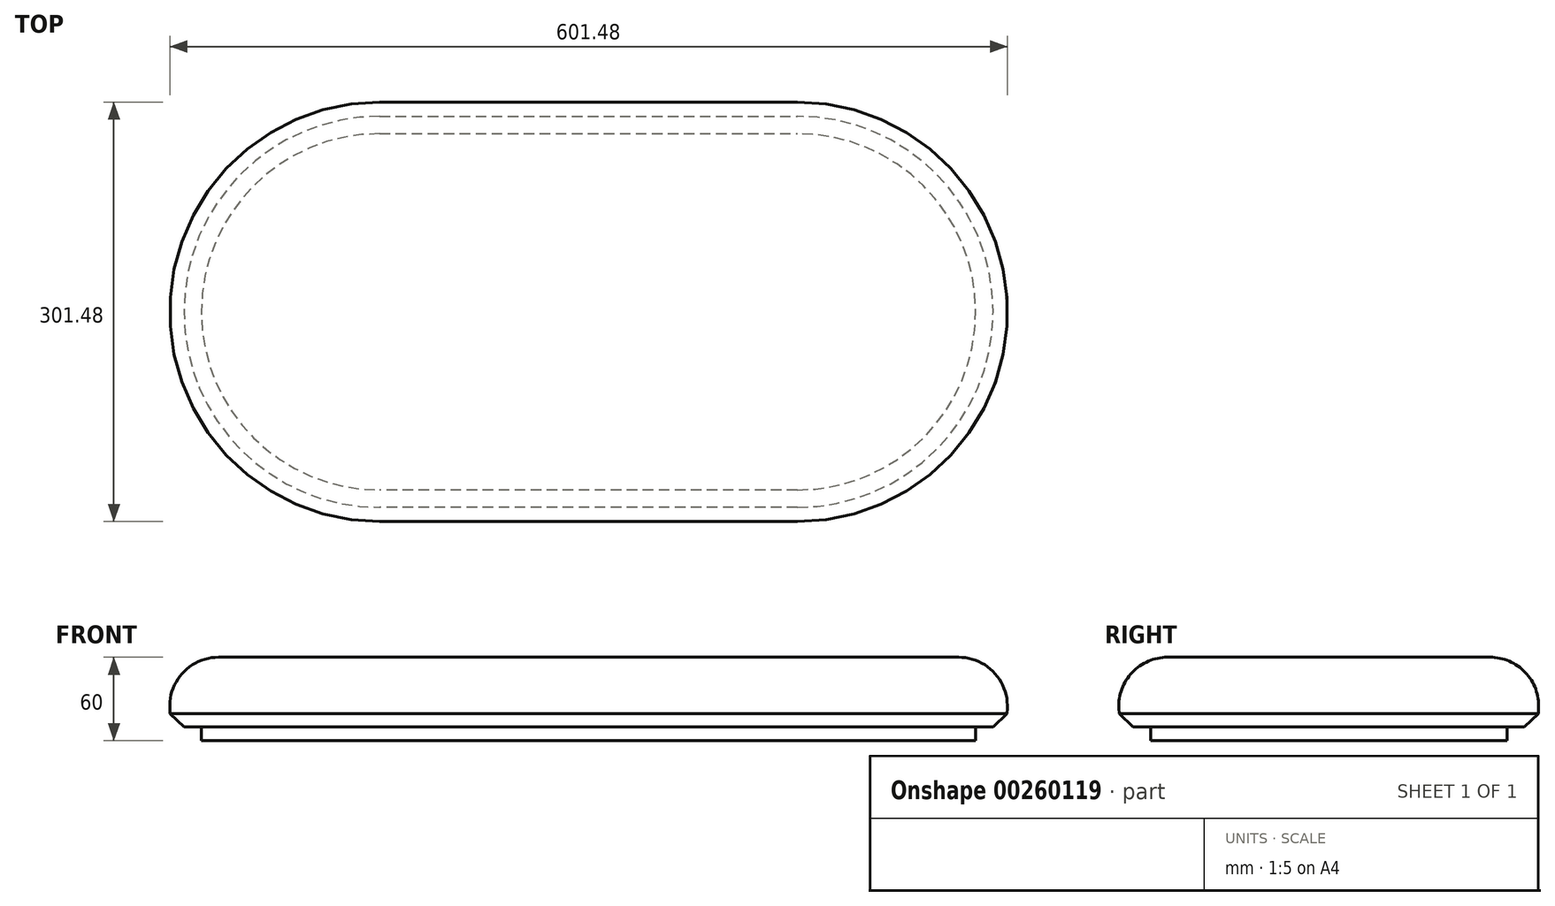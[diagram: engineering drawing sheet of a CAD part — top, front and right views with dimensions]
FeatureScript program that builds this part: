
annotation { "Feature Type Name" : "Feature", "Feature Type Description" : "" }
export const myFeature = defineFeature(function(context is Context, id is Id, definition is map)
    precondition{}
    {
        {
            var Q0;
            Q0=qCreatedBy(makeId("Top.planeOp"),FACE);
            var sketch = newSketch(context, id + "F0", { "sketchPlane" : qUnion([Q0])});
            skLineSegment(sketch, "E0.bottom", {"start": v(150, 150) * mm, "end": v(-150, 150) * mm});
            skLineSegment(sketch, "E0.top", {"start": v(150, -150) * mm, "end": v(-150, -150) * mm});
            skPoint(sketch, "E0.middle", {"position": v(0, 0) * mm});
            skArc(sketch, "E1", {"start": v(150, -150) * mm, "mid": v(300, 0) * mm, "end": v(150, 150) * mm});
            skArc(sketch, "E2", {"start": v(-150, -150) * mm, "mid": v(-300, 0) * mm, "end": v(-150, 150) * mm});
            skSolve(sketch);
        }
        {
            var Q0;
            Q0 = qSketchRegion(id + "F0", true);
            extrude(context, id + "F1", {"entities" : qUnion([Q0]), "depth" : 50 * mm, "hasDraft" : true, "draftAngle" : 3 * degree});
        }
        {
            var Q0;
            Q0=makeQuery(id+"F1.opExtrude","CAP_FACE",FACE,{"disambiguationData":[OSD([sQuery(id+"F0.wireOp",EDGE,"E0.bottom"),sQuery(id+"F0.wireOp",EDGE,"E0.top"),sQuery(id+"F0.wireOp",EDGE,"E1"),sQuery(id+"F0.wireOp",EDGE,"E2")])],"isStart":false});
            fillet(context, id + "F2", {"entities" : qUnion([Q0]), "radius" : 35 * mm, "tangentPropagation" : true, "allowEdgeOverflow" : false});
        }
        {
            var Q0;
            Q0=makeQuery(id+"F1.opExtrude","CAP_FACE",FACE,{"disambiguationData":[OSD([sQuery(id+"F0.wireOp",EDGE,"E0.bottom"),sQuery(id+"F0.wireOp",EDGE,"E0.top"),sQuery(id+"F0.wireOp",EDGE,"E1"),sQuery(id+"F0.wireOp",EDGE,"E2")])],"isStart":true});
            chamfer(context, id + "F3", {"entities" : qUnion([Q0]), "width" : 10 * mm, "tangentPropagation" : true});
        }
        {
            var Q0;
            Q0=makeQuery(id+"F1.opExtrude","CAP_FACE",FACE,{"disambiguationData":[OSD([sQuery(id+"F0.wireOp",EDGE,"E0.bottom"),sQuery(id+"F0.wireOp",EDGE,"E0.top"),sQuery(id+"F0.wireOp",EDGE,"E1"),sQuery(id+"F0.wireOp",EDGE,"E2")])],"isStart":true});
            var sketch = newSketch(context, id + "F4", { "sketchPlane" : qUnion([Q0])});
            skArc(sketch, "E3.0", {"start": v(-150, 128) * mm, "mid": v(-278, 0) * mm, "end": v(-150, -128) * mm});
            skLineSegment(sketch, "E3.1", {"start": v(150, 128) * mm, "end": v(-150, 128) * mm});
            skArc(sketch, "E3.2", {"start": v(150, -128) * mm, "mid": v(278, 0) * mm, "end": v(150, 128) * mm});
            skLineSegment(sketch, "E3.3", {"start": v(-150, -128) * mm, "end": v(150, -128) * mm});
            skSolve(sketch);
        }
        {
            var Q0;
            Q0 = qSketchRegion(id + "F4", true);
            extrude(context, id + "F5", {"entities" : qUnion([Q0]), "operationType" : NewBodyOperationType.ADD, "depth" : 10 * mm});
        }
    });
